# Revit family: Barrera optica infrarroja_Aguilera Electronica
name_source: partatom
category: Dispositivos de alarma de incendios
units: mm (PartAtom-declared; Revit-internal decimal feet)

## family parameters
Anfitrión = Cara
Compartido = No
Corte con vacíos al cargar = No
Cota de conector redondo = Diámetro de uso
Mantener orientación de anotación = Sí
Número OmniClass = 23.85.30.21.11.11.11
Punto de cálculo de habitación = No
Tipo de pieza = Normal
Título OmniClass = Smoke Detectors

## types (1)
- Barrera óptica infrarroja
    Altura transmisor / receptor = 78 mm  [stored 0.255906 ft]
    Altura unidad control = 203 mm  [stored 0.66601 ft]
    Ancho transmisor / receptor = 77 mm  [stored 0.252625 ft]
    Ancho unidad control = 124 mm  [stored 0.406824 ft]
    Comentarios de tipo = El sistema se compone de un moderno transmisor que emite un haz estrecho de luz infrarroja a un receptor asociado, y un controlador de bajo nivel compacto. Cuando el humo atraviesa la trayectoria del haz de infrarrojos, la intensidad de la señal en el receptor disminuye. Por debajo de un nivel preestablecido, el equipo pasa a condición de alarma.
Tanto el transmisor como el receptor llevan integrados discos giratorios para facilitar su alineación. Usando estos discos giratorios el proceso de ajuste fino se realiza de una manera suave y fiable. Cada equipo permite un ajuste de 10 grados en ambos planos.
Para un ajuste mayor se disponen de soportes adicionales que proporcionan un movimiento máximo de 180 grados en ambos planos, así como una rotación completa de 360 grados.
El detector lineal de humo de rayos infrarrojos AE/BO3000 ha sido diseñado para que pueda ser instalado por un único operador, utilizando la alineación asistida por el láser incorporado en el receptor, y un conjunto de indicadores luminosos que indican el punto de alineación óptimo.
El detector lineal de humo de rayos infrarrojos AE/BO3000 también tiene una característica que permite que el transmisor sea alimentado desde el controlador directamente, reduciendo el número de fuentes de alimentación necesarias.
El controlador de bajo nivel incorpora una pantalla LCD, que ofrece una interface basada en iconos y fácil de usar. Este controlador facilita la puesta en marcha, pruebas y mantenimiento del sistema de detección. Durante la puesta en marcha, los umbrales de sensibilidad al fuego del detector pueden ser seleccionados directamente, así como tiempos de paso a alarma y avería del equipo.
El detector es totalmente compatible con los requisitos de RoHS y WEEE.
    Descripción = El detector lineal de humo de rayos infrarrojos AE/BO3000 ha sido diseñado utilizando la última tecnología óptica de detección de incendios. Este detector ofrece una protección eficaz para grandes espacios abiertos con techos altos. Muy adecuado también para aplicaciones donde la instalación de detectores puntuales de humo presenta dificultades.
El detector lineal de humo de rayos infrarrojos AE/BO3000 es ideal para aplicaciones donde la línea de visión para el IR (Infrarrojo) es estrecha y donde la estructura del edificio utiliza superficies reflectantes. También ha sido diseñado para ser estéticamente agradable y, por lo tanto, integrable en los edificios arquitectónicos modernos, así como en sitios patrimoniales, y en particular donde existen techos ornamentales.
Certificado EN 54-12 y UL268
    Elevación por defecto = 400 mm  [stored 1.31234 ft]
    Fabricante = Aguilera Electrónica
    Modelo = AE/BO3000
    Profundidad transmisor / receptor = 161 mm  [stored 0.528215 ft]
    Profundidad unidad control = 72 mm  [stored 0.23622 ft]
    Símbolo = Sí
    Símbolo texto modelo = Sí
    URL = https://aguilera.es

note: [stored X ft] marks values corroborated as IEEE doubles in the binary element streams (Revit-internal decimal feet)
